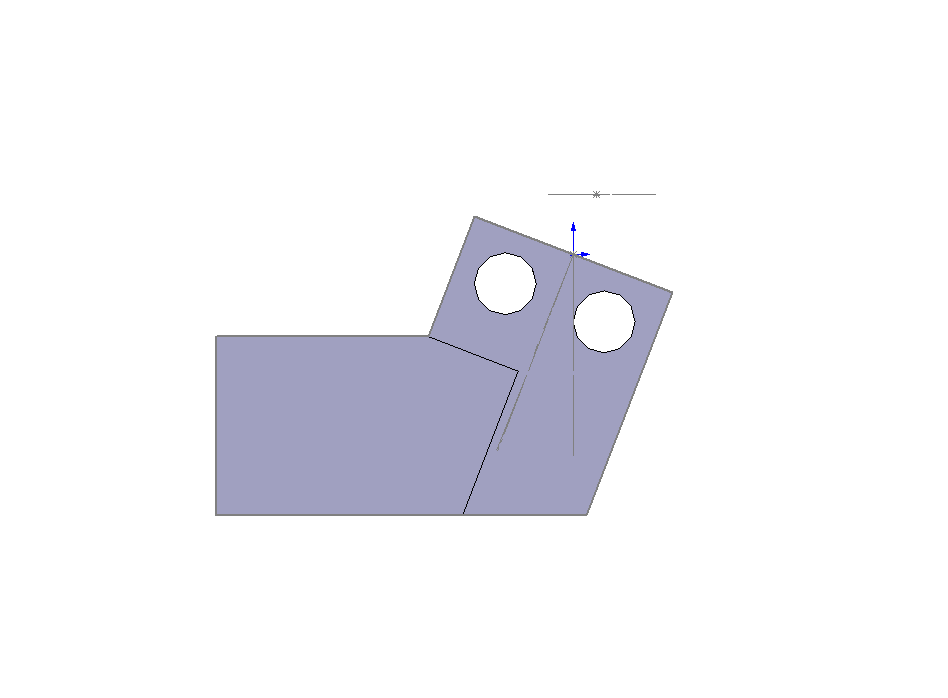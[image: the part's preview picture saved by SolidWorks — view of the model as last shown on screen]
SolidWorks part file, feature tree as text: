
SOLIDWORKS PART (.sldprt)
format: sldprt  version: not decoded by parser v0  size: 317,952 bytes
history: native  units: mm
features: sketch x4, cut_extrude x3, material x1, extrude x1 (+12 scaffold rows collapsed)
feature tree (21):
  scaffold x12  (default folders/planes/origin — collapsed)
  material  "Material <not specified>"
  sketch  "Sketch1"  dims[c1.D1=~23.614254mm c2.D1=21.07deg c2.D2=16.51mm c2.D3=17.78mm c2.D4=16.0mm c2.D5=13.9mm c3.D2=17.78mm c3.D3=16.51mm c4.D2=16.51mm c4.D6=8.0mm c4.D7=4.0mm c5.D6=12.0mm c5.D7=10.0mm c6.D6=3.35mm c6.D7=~30.015838mm c6.D4=25.0mm c7.D6=5.07mm]
  extrude  "Base-Extrude"  Depth=10mm
  sketch  "Sketch2"  dims[D1=10.0mm D2=9.0mm]
  cut_extrude  "Cutaway for Clamp Plate & Wire"  Depth=5mm
  sketch  "Sketch3"  dims[c1.D1=4.826mm c1.D4=4.572mm c1.D2=8.0mm c2.D2=90.0deg c2.D3=~4.003032mm c2.D4=4.1275mm c2.D5=8.255mm c3.D3=4.0mm]
  cut_extrude  "Clamp Plate Holes (altered to #10-24 OCT04)"  [1 undecoded]
  sketch  "Sketch4"  dims[D1=4.572mm D2=8.255mm]
  cut_extrude  "Holes to Pitch Plate"  [1 undecoded]
decode coverage: 6 of 8 modeling features carry decoded parameters
note: ~ marks probable driven/reference dimensions
note: 2 parameter values undecoded
note: suppression state not decoded; provenance and decode notes live in map.json
